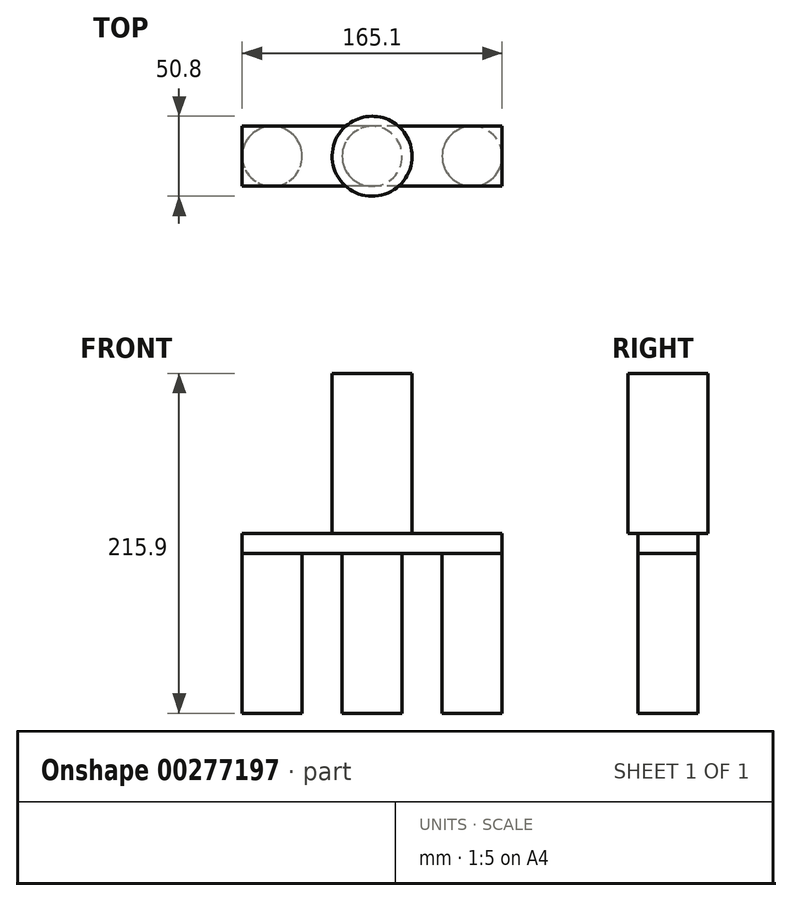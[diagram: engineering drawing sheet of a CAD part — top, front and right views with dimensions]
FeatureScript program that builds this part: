
annotation { "Feature Type Name" : "Feature", "Feature Type Description" : "" }
export const myFeature = defineFeature(function(context is Context, id is Id, definition is map)
    precondition{}
    {
        {
            var Q0;
            Q0=qCreatedBy(makeId("Top.planeOp"),FACE);
            var sketch = newSketch(context, id + "F0", { "sketchPlane" : qUnion([Q0])});
            skLineSegment(sketch, "E0.bottom", {"start": v(82.55, 19.05) * mm, "end": v(-82.55, 19.05) * mm});
            skLineSegment(sketch, "E0.top", {"start": v(82.55, -19.05) * mm, "end": v(-82.55, -19.05) * mm});
            skLineSegment(sketch, "E0.left", {"start": v(82.55, 19.05) * mm, "end": v(82.55, -19.05) * mm});
            skLineSegment(sketch, "E0.right", {"start": v(-82.55, 19.05) * mm, "end": v(-82.55, -19.05) * mm});
            skPoint(sketch, "E0.middle", {"position": v(0, 0) * mm});
            skSolve(sketch);
        }
        {
            var Q0;
            Q0 = qSketchRegion(id + "F0", true);
            extrude(context, id + "F1", {"entities" : qUnion([Q0]), "depth" : 12.7 * mm});
        }
        {
            var Q0;
            Q0=makeQuery(id+"F1.opExtrude","CAP_FACE",FACE,{"disambiguationData":[OSD([sQuery(id+"F0.wireOp",EDGE,"E0.bottom"),sQuery(id+"F0.wireOp",EDGE,"E0.top"),sQuery(id+"F0.wireOp",EDGE,"E0.left"),sQuery(id+"F0.wireOp",EDGE,"E0.right")])],"isStart":false});
            var sketch = newSketch(context, id + "F2", { "sketchPlane" : qUnion([Q0])});
            skCircle(sketch, "E1", {"center": v(0, 0) * mm, "radius": 25.4 * mm});
            skSolve(sketch);
        }
        {
            var Q0;
            Q0 = qSketchRegion(id + "F2", true);
            extrude(context, id + "F3", {"entities" : qUnion([Q0]), "operationType" : NewBodyOperationType.ADD, "depth" : 101.6 * mm});
        }
        {
            var Q0;
            Q0=makeQuery(id+"F1.opExtrude","CAP_FACE",FACE,{"disambiguationData":[OSD([sQuery(id+"F0.wireOp",EDGE,"E0.bottom"),sQuery(id+"F0.wireOp",EDGE,"E0.top"),sQuery(id+"F0.wireOp",EDGE,"E0.left"),sQuery(id+"F0.wireOp",EDGE,"E0.right")])],"isStart":true});
            var sketch = newSketch(context, id + "F4", { "sketchPlane" : qUnion([Q0])});
            skCircle(sketch, "E2", {"center": v(0, 0) * mm, "radius": 19.05 * mm});
            skCircle(sketch, "E3", {"center": v(63.5, 0) * mm, "radius": 19.05 * mm});
            skCircle(sketch, "E4", {"center": v(-63.5, 0) * mm, "radius": 19.05 * mm});
            skSolve(sketch);
        }
        {
            var Q0;
            {var subQ0=sQuery(id+"F4.wireOp",EDGE,"E2");var subQ1=makeQuery(id+"F4.imprint","INTERSECT",VERTEX,{"derivedFrom":[makeQuery(id+"F1.opExtrude","CAP_EDGE",EDGE,{"disambiguationData":[OSD([sQuery(id+"F0.wireOp",EDGE,"E0.bottom")])],"isStart":true}),subQ0]});Q0=makeQuery(id+"F4.imprint","IMPRINT",FACE,{"disambiguationData":[TD([[makeQuery(id+"F4.imprint","IMPRINT",EDGE,{"disambiguationData":[TD([[subQ1,1.0]])],"derivedFrom":subQ0}),1.0]])]});}
            var Q1;
            {var subQ0=sQuery(id+"F4.wireOp",EDGE,"E3");var subQ1=makeQuery(id+"F4.imprint","INTERSECT",VERTEX,{"derivedFrom":[makeQuery(id+"F1.opExtrude","CAP_EDGE",EDGE,{"disambiguationData":[OSD([sQuery(id+"F0.wireOp",EDGE,"E0.top")])],"isStart":true}),subQ0]});Q1=makeQuery(id+"F4.imprint","IMPRINT",FACE,{"disambiguationData":[TD([[makeQuery(id+"F4.imprint","IMPRINT",EDGE,{"disambiguationData":[TD([[subQ1,1.0]])],"derivedFrom":subQ0}),1.0]])]});}
            var Q2;
            {var subQ0=sQuery(id+"F4.wireOp",EDGE,"E4");var subQ1=makeQuery(id+"F4.imprint","INTERSECT",VERTEX,{"derivedFrom":[makeQuery(id+"F1.opExtrude","CAP_EDGE",EDGE,{"disambiguationData":[OSD([sQuery(id+"F0.wireOp",EDGE,"E0.right")])],"isStart":true}),subQ0]});Q2=makeQuery(id+"F4.imprint","IMPRINT",FACE,{"disambiguationData":[TD([[makeQuery(id+"F4.imprint","IMPRINT",EDGE,{"disambiguationData":[TD([[subQ1,1.0]])],"derivedFrom":subQ0}),1.0]])]});}
            extrude(context, id + "F5", {"entities" : qUnion([Q0, Q1, Q2]), "operationType" : NewBodyOperationType.ADD, "depth" : 101.6 * mm});
        }
    });
